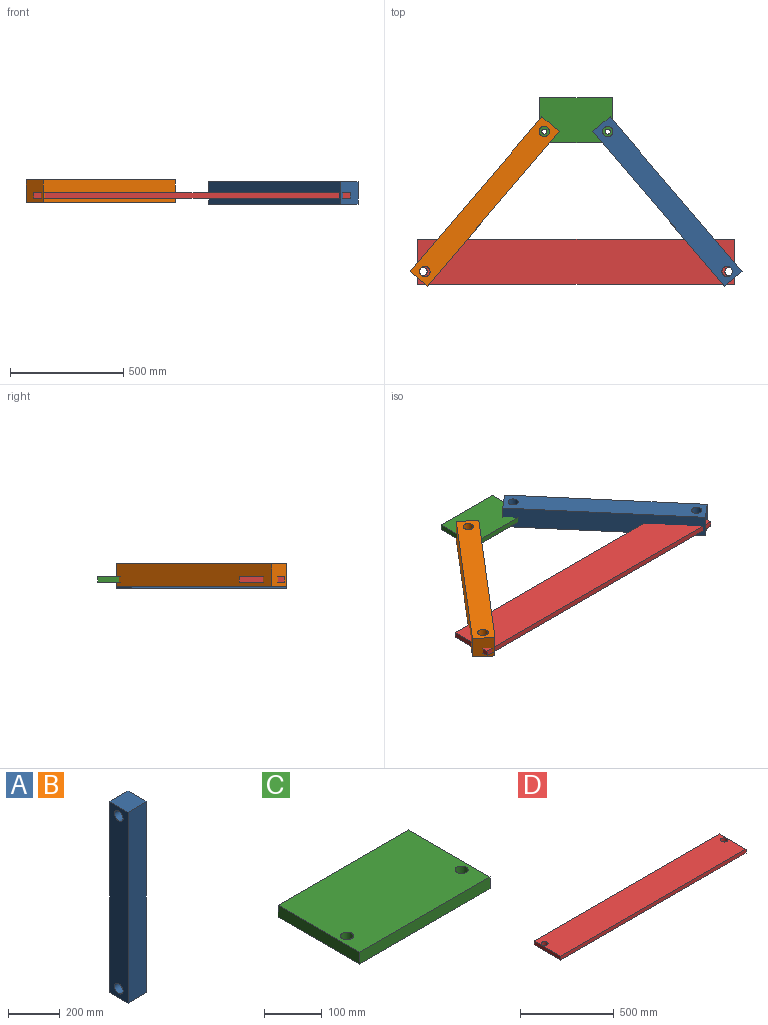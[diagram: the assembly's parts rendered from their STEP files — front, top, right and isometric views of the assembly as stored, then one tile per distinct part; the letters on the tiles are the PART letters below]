
ASSEMBLY  parts=4 mates=5
PART A: 8 faces, bbox 100x100x900 mm
  f0: plane 900x100mm, normal (1,0,0), area 86672.3mm2, adj f2,f3,f4,f5,f6,f7
  f1: plane 900x100mm, normal (-1,0,0), area 86672.3mm2, adj f2,f3,f4,f5,f6,f7
  f2: plane 900x100mm, normal (0,-1,0), area 90000mm2, adj f0,f1,f4,f5
  f3: plane 900x100mm, normal (0,1,0), area 90000mm2, adj f0,f1,f4,f5
  f4: plane 100x100mm, normal (0,0,1), area 10000mm2, adj f0,f1,f2,f3
  f5: plane 100x100mm, normal (0,0,-1), area 10000mm2, adj f0,f1,f2,f3
  f6: cylinder r=23.01mm len=100mm, axis (-1,0,0), area 14459.8mm2, adj f0,f1
  f7: cylinder r=23.01mm len=100mm, axis (-1,0,0), area 14459.8mm2, adj f0,f1
PART B: same geometry as A
PART C: 8 faces, bbox 320x200x25 mm
  f0: plane 320x200mm, normal (0,0,1), area 63195.3mm2, adj f2,f3,f4,f5,f6,f7
  f1: plane 320x200mm, normal (0,0,-1), area 63195.3mm2, adj f2,f3,f4,f5,f6,f7
  f2: plane 320x25mm, normal (0,1,0), area 8000mm2, adj f0,f1,f3,f5
  f3: plane 200x25mm, normal (-1,0,0), area 5000mm2, adj f0,f1,f2,f4
  f4: plane 320x25mm, normal (0,-1,0), area 8000mm2, adj f0,f1,f3,f5
  f5: plane 200x25mm, normal (1,0,0), area 5000mm2, adj f0,f1,f2,f4
  f6: cylinder r=11.32mm len=25mm, axis (0,0,1), area 1777.7mm2, adj f0,f1
  f7: cylinder r=11.32mm len=25mm, axis (0,0,1), area 1777.7mm2, adj f0,f1
PART D: 8 faces, bbox 1400x200x25 mm
  f0: plane 1400x200mm, normal (0,0,1), area 277775.6mm2, adj f2,f3,f4,f5,f6,f7
  f1: plane 1400x200mm, normal (0,0,-1), area 277775.6mm2, adj f2,f3,f4,f5,f6,f7
  f2: plane 1400x25mm, normal (0,1,0), area 35000mm2, adj f0,f1,f3,f5
  f3: plane 200x25mm, normal (-1,0,0), area 5000mm2, adj f0,f1,f2,f4
  f4: plane 1400x25mm, normal (0,-1,0), area 35000mm2, adj f0,f1,f3,f5
  f5: plane 200x25mm, normal (1,0,0), area 5000mm2, adj f0,f1,f2,f4
  f6: cylinder r=18.82mm len=37.63mm, axis (0,0,1), area 2955.5mm2, adj f0,f1
  f7: cylinder r=18.82mm len=37.63mm, axis (0,0,1), area 2955.5mm2, adj f0,f1
PLACE A rot(axis=(-0.39,-0.84,-0.39),100.1deg) t=(77.2,-548.52,23.83)mm
PLACE B rot(axis=(-0.67,-0.31,-0.67),145.5deg) t=(-1315.59,-548.52,31.17)mm
PLACE C t=(-219.66,-56.97,0)mm fixed
PLACE D rot(axis=(0,0,-1),180deg) t=(291.35,-1.42,0)mm
MATE cylindrical A.f7 <-> C.f6  axis (0,0,-1) through (-478.7,103.73,-26.17)mm
MATE cylindrical D.f1 <-> A.f6  axis (0,0,-1) through (49.3,-515.79,0)mm
MATE cylindrical B.f6 <-> D.f1  axis (0,0,1) through (-1287.7,-515.79,81.17)mm
MATE cylindrical B.f7 <-> C.f7  axis (0,0,-1) through (-759.7,103.73,-18.83)mm
MATE parallel C.f2 <-> D.f2  axis (0,1,0) through (-619.2,253.73,12.5)mm
